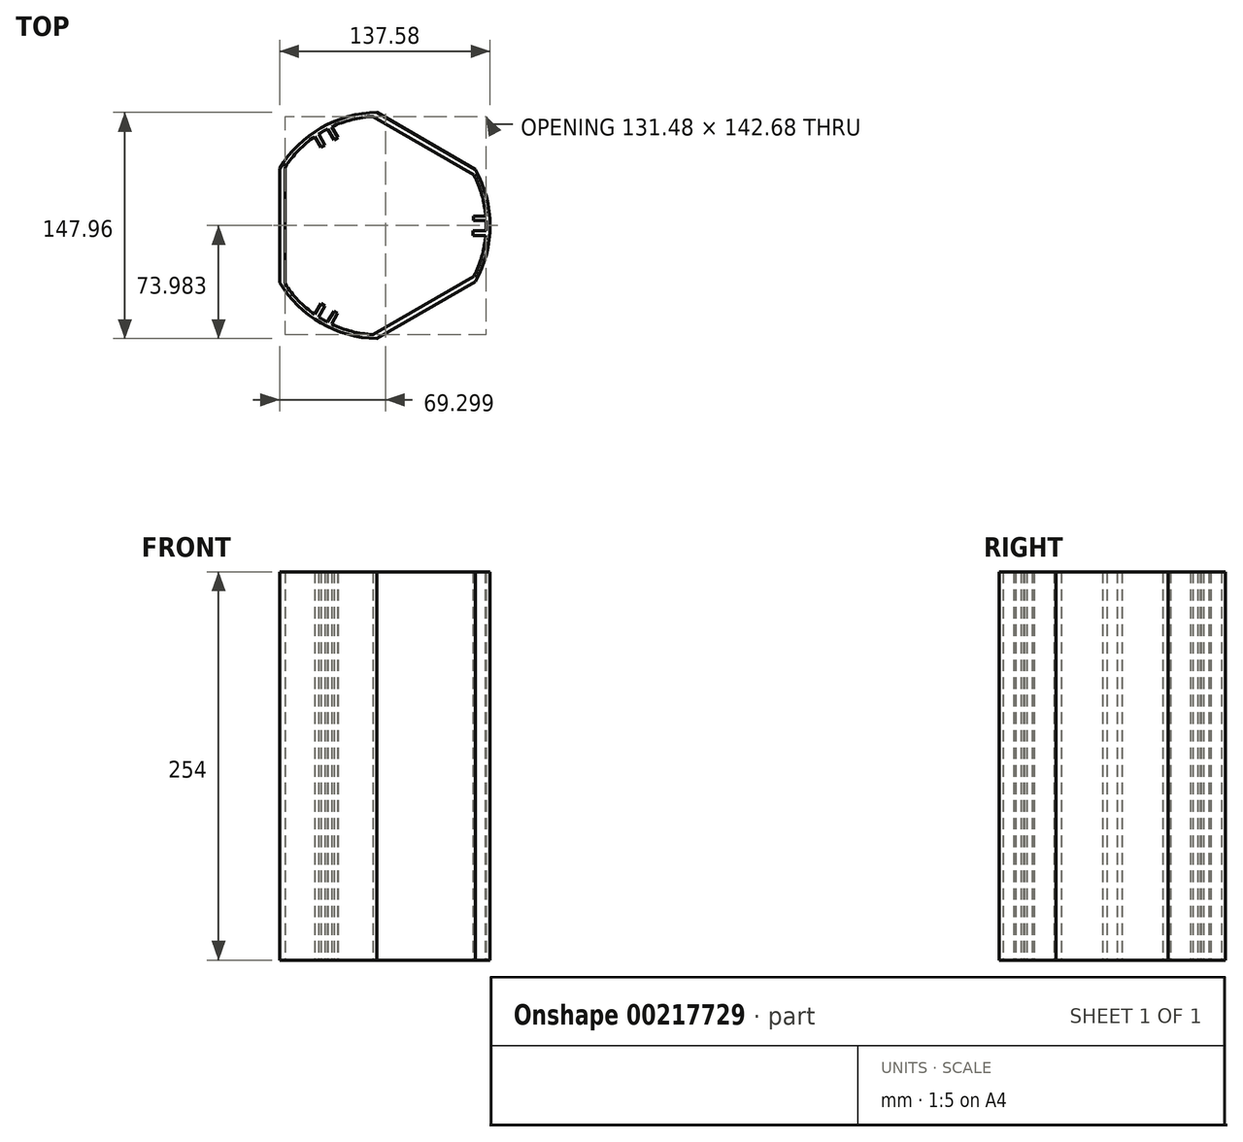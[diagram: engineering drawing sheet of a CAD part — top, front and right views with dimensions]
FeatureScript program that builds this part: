
annotation { "Feature Type Name" : "Feature", "Feature Type Description" : "" }
export const myFeature = defineFeature(function(context is Context, id is Id, definition is map)
    precondition{}
    {
        {
            var Q0;
            Q0=qCreatedBy(makeId("Top.planeOp"),FACE);
            var sketch = newSketch(context, id + "F0", { "sketchPlane" : qUnion([Q0])});
            skPoint(sketch, "E0.second.point", {"position": v(62.23, 0) * mm});
            skPoint(sketch, "E0.third.point", {"position": v(30, 27.57) * mm});
            skPoint(sketch, "E1.center", {"position": v(34.29, -0.04) * mm});
            skLineSegment(sketch, "E2", {"start": v(15.32, 43.04) * mm, "end": v(15.27, 43.25) * mm});
            skLineSegment(sketch, "E3", {"start": v(29.61, 34.8) * mm, "end": v(29.8, 34.84) * mm});
            skLineSegment(sketch, "E4", {"start": v(29.61, -34.8) * mm, "end": v(29.8, -34.83) * mm});
            skPoint(sketch, "E5.startSnap0", {"position": v(-57.75, 29.6) * mm});
            skLineSegment(sketch, "E6.0", {"start": v(-2.84, 71.35) * mm, "end": v(63.24, 33.1) * mm});
            skLineSegment(sketch, "E6.1", {"start": v(-60.28, 38.27) * mm, "end": v(-60.36, -38.13) * mm});
            skLineSegment(sketch, "E6.2", {"start": v(-3, -71.34) * mm, "end": v(63.24, -33.2) * mm});
            skLineSegment(sketch, "E7.0", {"start": v(-0.3, 73.98) * mm, "end": v(64.26, 36.61) * mm});
            skLineSegment(sketch, "E7.1", {"start": v(-63.84, 37.4) * mm, "end": v(-63.92, -37.25) * mm});
            skLineSegment(sketch, "E7.2", {"start": v(-0.47, -73.98) * mm, "end": v(64.26, -36.71) * mm});
            skLineSegment(sketch, "E8", {"start": v(-35.38, -61.11) * mm, "end": v(-38.56, -66.6) * mm});
            skArc(sketch, "E9", {"start": v(64.26, -36.71) * mm, "mid": v(73.66, -0.05) * mm, "end": v(64.26, 36.61) * mm});
            skArc(sketch, "E10", {"start": v(-0.3, 73.98) * mm, "mid": v(-36.76, 63.83) * mm, "end": v(-63.84, 37.4) * mm});
            skArc(sketch, "E11.0", {"start": v(-2.84, 71.35) * mm, "mid": v(-16.67, 69.24) * mm, "end": v(-29.85, 64.57) * mm});
            skArc(sketch, "E12", {"start": v(-63.92, -37.25) * mm, "mid": v(-36.9, -63.75) * mm, "end": v(-0.47, -73.98) * mm});
            skArc(sketch, "E13.0", {"start": v(-60.36, -38.13) * mm, "mid": v(-51.63, -49.06) * mm, "end": v(-40.99, -58.13) * mm});
            skArc(sketch, "E14.0", {"start": v(63.24, -33.2) * mm, "mid": v(68.32, -20.17) * mm, "end": v(70.84, -6.43) * mm});
            skLineSegment(sketch, "E15.0", {"start": v(70.62, 6.27) * mm, "end": v(62.69, 6.28) * mm});
            skLineSegment(sketch, "E16.0", {"start": v(70.6, -6.43) * mm, "end": v(62.68, -6.42) * mm});
            skLineSegment(sketch, "E17", {"start": v(70.62, 6.27) * mm, "end": v(70.85, 6.27) * mm});
            skLineSegment(sketch, "E18", {"start": v(70.6, -6.43) * mm, "end": v(70.84, -6.43) * mm});
            skLineSegment(sketch, "E19", {"start": v(62.69, 3.36) * mm, "end": v(62.69, 6.28) * mm});
            skPoint(sketch, "E20.orphan", {"position": v(71.16, -6.42) * mm});
            skLineSegment(sketch, "E21", {"start": v(62.68, -3.5) * mm, "end": v(62.68, -6.42) * mm});
            skPoint(sketch, "E22.orphan", {"position": v(62.04, -6.42) * mm});
            skLineSegment(sketch, "E23.0", {"start": v(70.62, 3.35) * mm, "end": v(62.69, 3.36) * mm});
            skLineSegment(sketch, "E24.0", {"start": v(70.6, -3.5) * mm, "end": v(62.68, -3.5) * mm});
            skLineSegment(sketch, "E25", {"start": v(70.62, 3.35) * mm, "end": v(71.04, 3.35) * mm});
            skLineSegment(sketch, "E26", {"start": v(70.6, -3.5) * mm, "end": v(71.04, -3.5) * mm});
            skArc(sketch, "E27.trimOffspring", {"start": v(70.85, 6.27) * mm, "mid": v(68.33, 20.04) * mm, "end": v(63.24, 33.1) * mm});
            skArc(sketch, "E28.trimOffspring", {"start": v(71.04, -3.5) * mm, "mid": v(71.12, -0.08) * mm, "end": v(71.04, 3.35) * mm});
            skLineSegment(sketch, "E29.0", {"start": v(-29.88, -64.3) * mm, "end": v(-25.9, -57.43) * mm});
            skLineSegment(sketch, "E30.0", {"start": v(-32.4, -62.83) * mm, "end": v(-28.44, -55.97) * mm});
            skLineSegment(sketch, "E31.0", {"start": v(-40.87, -57.93) * mm, "end": v(-36.9, -51.07) * mm});
            skLineSegment(sketch, "E32.0", {"start": v(-38.34, -59.4) * mm, "end": v(-34.37, -52.53) * mm});
            skLineSegment(sketch, "E33", {"start": v(-33.83, -52.1) * mm, "end": v(-34.15, -52.66) * mm});
            skLineSegment(sketch, "E34", {"start": v(-34.37, -52.53) * mm, "end": v(-36.9, -51.07) * mm});
            skLineSegment(sketch, "E35", {"start": v(-28.34, -55.3) * mm, "end": v(-28.66, -55.84) * mm});
            skLineSegment(sketch, "E36", {"start": v(-28.44, -55.97) * mm, "end": v(-25.9, -57.43) * mm});
            skLineSegment(sketch, "E37", {"start": v(-29.88, -64.3) * mm, "end": v(-30, -64.5) * mm});
            skLineSegment(sketch, "E38", {"start": v(-40.87, -57.93) * mm, "end": v(-40.99, -58.13) * mm});
            skLineSegment(sketch, "E39", {"start": v(-38.34, -59.4) * mm, "end": v(-38.56, -59.76) * mm});
            skLineSegment(sketch, "E40", {"start": v(-32.4, -62.83) * mm, "end": v(-32.62, -63.2) * mm});
            skArc(sketch, "E41.trimOffspring", {"start": v(-38.56, -59.76) * mm, "mid": v(-35.63, -61.55) * mm, "end": v(-32.62, -63.2) * mm});
            skArc(sketch, "E42.trimOffspring", {"start": v(-30, -64.5) * mm, "mid": v(-16.82, -69.2) * mm, "end": v(-3, -71.34) * mm});
            skLineSegment(sketch, "E43.0", {"start": v(-40.74, 58.02) * mm, "end": v(-36.78, 51.16) * mm});
            skLineSegment(sketch, "E44.0", {"start": v(-29.73, 64.36) * mm, "end": v(-25.78, 57.5) * mm});
            skLineSegment(sketch, "E45.0", {"start": v(-38.2, 59.48) * mm, "end": v(-34.25, 52.62) * mm});
            skLineSegment(sketch, "E46.0", {"start": v(-32.26, 62.9) * mm, "end": v(-28.3, 56.04) * mm});
            skLineSegment(sketch, "E47", {"start": v(-34.25, 52.62) * mm, "end": v(-36.78, 51.16) * mm});
            skLineSegment(sketch, "E48", {"start": v(-40.74, 58.02) * mm, "end": v(-40.85, 58.23) * mm});
            skLineSegment(sketch, "E49", {"start": v(-28.3, 56.04) * mm, "end": v(-25.78, 57.5) * mm});
            skLineSegment(sketch, "E50", {"start": v(-29.73, 64.36) * mm, "end": v(-29.85, 64.57) * mm});
            skLineSegment(sketch, "E51", {"start": v(-32.26, 62.9) * mm, "end": v(-32.48, 63.27) * mm});
            skLineSegment(sketch, "E52", {"start": v(-38.2, 59.48) * mm, "end": v(-38.42, 59.85) * mm});
            skArc(sketch, "E53.trimOffspring", {"start": v(-40.85, 58.23) * mm, "mid": v(-51.52, 49.17) * mm, "end": v(-60.28, 38.27) * mm});
            skArc(sketch, "E54.trimOffspring", {"start": v(-32.48, 63.27) * mm, "mid": v(-35.49, 61.63) * mm, "end": v(-38.42, 59.85) * mm});
            skSolve(sketch);
        }
        {
            var Q0;
            Q0 = qSketchRegion(id + "F0", true);
            extrude(context, id + "F1", {"entities" : qUnion([Q0]), "depth" : 254 * mm});
        }
    });
